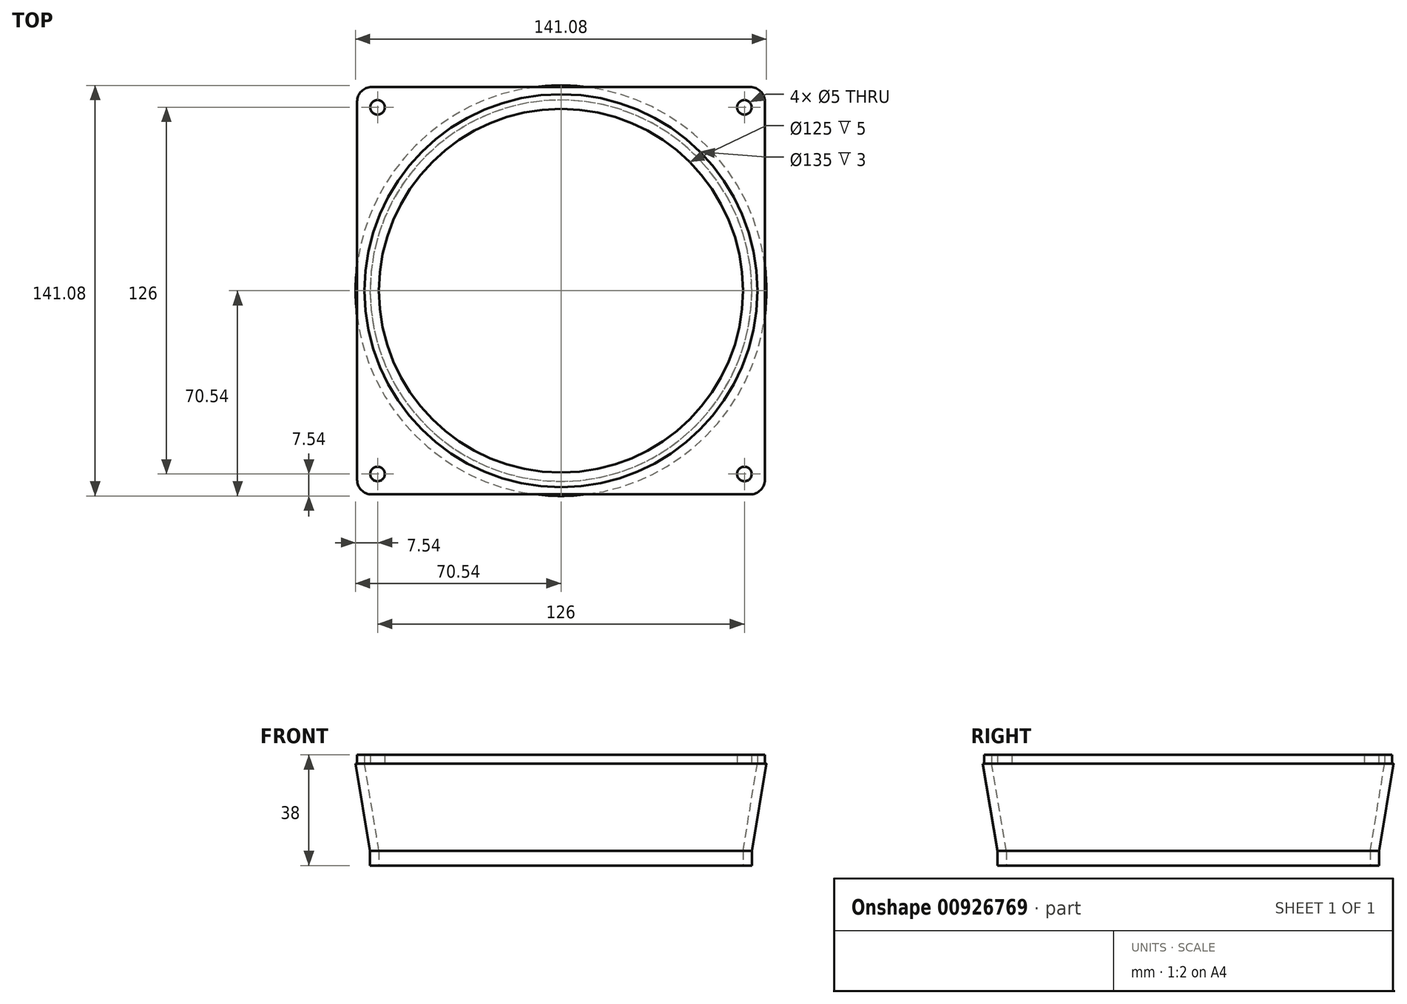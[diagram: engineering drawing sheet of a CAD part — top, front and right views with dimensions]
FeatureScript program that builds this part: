
annotation { "Feature Type Name" : "Feature", "Feature Type Description" : "" }
export const myFeature = defineFeature(function(context is Context, id is Id, definition is map)
    precondition{}
    {
        {
            var Q0;
            Q0=qCreatedBy(makeId("Front.planeOp"),FACE);
            var sketch = newSketch(context, id + "F0", { "sketchPlane" : qUnion([Q0])});
            skLineSegment(sketch, "E0", {"start": v(0, 0) * mm, "end": v(-62.5, 0) * mm, "construction": true});
            skLineSegment(sketch, "E1", {"start": v(0, 30) * mm, "end": v(-67.5, 30) * mm, "construction": true});
            skLineSegment(sketch, "E2", {"start": v(-62.5, 0) * mm, "end": v(-67.5, 30) * mm});
            skLineSegment(sketch, "E3.0", {"start": v(-65.54, 0) * mm, "end": v(-70.54, 30) * mm});
            skLineSegment(sketch, "E4", {"start": v(-67.5, 30) * mm, "end": v(-70.54, 30) * mm});
            skLineSegment(sketch, "E5", {"start": v(-62.5, 0) * mm, "end": v(-65.54, 0) * mm});
            skLineSegment(sketch, "E6", {"start": v(-65.54, 0) * mm, "end": v(-65.54, -5) * mm});
            skLineSegment(sketch, "E7", {"start": v(-65.54, -5) * mm, "end": v(-62.5, -5) * mm});
            skLineSegment(sketch, "E8", {"start": v(-62.5, 0) * mm, "end": v(-62.5, -5) * mm});
            skLineSegment(sketch, "E9", {"start": v(0, -41.93) * mm, "end": v(0, 55.66) * mm, "construction": true});
            skSolve(sketch);
        }
        {
            var Q0;
            Q0=makeQuery(id+"F0.imprint","IMPRINT",FACE,{"disambiguationData":[TD([[makeQuery(id+"F0.imprint","IMPRINT",EDGE,{"derivedFrom":sQuery(id+"F0.wireOp",EDGE,"E2")}),1.0]])]});
            var Q1;
            Q1=makeQuery(id+"F0.imprint","IMPRINT",FACE,{"disambiguationData":[TD([[makeQuery(id+"F0.imprint","IMPRINT",EDGE,{"derivedFrom":sQuery(id+"F0.wireOp",EDGE,"E5")}),1.0]])]});
            var Q2;
            Q2=sQuery(id+"F0.wireOp",EDGE,"E9");
            revolve(context, id + "F1", {"surfaceOperationType" : NewSurfaceOperationType.NEW, "entities" : qUnion([Q0, Q1]), "axis" : qUnion([Q2]), "revolveType" : RevolveType.FULL});
        }
        {
            var Q0;
            Q0=makeQuery(id+"F1.opRevolve","SWEPT_FACE",FACE,{"disambiguationData":[OSD([sQuery(id+"F0.wireOp",EDGE,"E4")])]});
            var sketch = newSketch(context, id + "F2", { "sketchPlane" : qUnion([Q0])});
            skLineSegment(sketch, "E10.bottom", {"start": v(-65, 70) * mm, "end": v(65, 70) * mm});
            skLineSegment(sketch, "E10.top", {"start": v(-65, -70) * mm, "end": v(65, -70) * mm});
            skLineSegment(sketch, "E10.left", {"start": v(-70, 65) * mm, "end": v(-70, -65) * mm});
            skLineSegment(sketch, "E10.right", {"start": v(70, 65) * mm, "end": v(70, -65) * mm});
            skCircle(sketch, "E11", {"center": v(-63, 63) * mm, "radius": 2.5 * mm});
            skCircle(sketch, "E12", {"center": v(63, 63) * mm, "radius": 2.5 * mm});
            skCircle(sketch, "E13", {"center": v(63, -63) * mm, "radius": 2.5 * mm});
            skCircle(sketch, "E14", {"center": v(-63, -63) * mm, "radius": 2.5 * mm});
            skPoint(sketch, "E15.visualSharp", {"position": v(70, -70) * mm});
            skArc(sketch, "E15.filletArc", {"start": v(65, -70) * mm, "mid": v(68.54, -68.54) * mm, "end": v(70, -65) * mm});
            skPoint(sketch, "E16.visualSharp", {"position": v(-70, -70) * mm});
            skArc(sketch, "E16.filletArc", {"start": v(-70, -65) * mm, "mid": v(-68.54, -68.54) * mm, "end": v(-65, -70) * mm});
            skPoint(sketch, "E17.visualSharp", {"position": v(-70, 70) * mm});
            skArc(sketch, "E17.filletArc", {"start": v(-65, 70) * mm, "mid": v(-68.54, 68.54) * mm, "end": v(-70, 65) * mm});
            skPoint(sketch, "E18.visualSharp", {"position": v(70, 70) * mm});
            skArc(sketch, "E18.filletArc", {"start": v(70, 65) * mm, "mid": v(68.54, 68.54) * mm, "end": v(65, 70) * mm});
            skCircle(sketch, "E19", {"center": v(0, 0) * mm, "radius": 67.5 * mm});
            skSolve(sketch);
        }
        {
            var Q0;
            Q0 = qSketchRegion(id + "F2", true);
            extrude(context, id + "F3", {"entities" : qUnion([Q0]), "operationType" : NewBodyOperationType.ADD, "depth" : 3 * mm, "offsetDistance" : 25 * mm});
        }
    });
